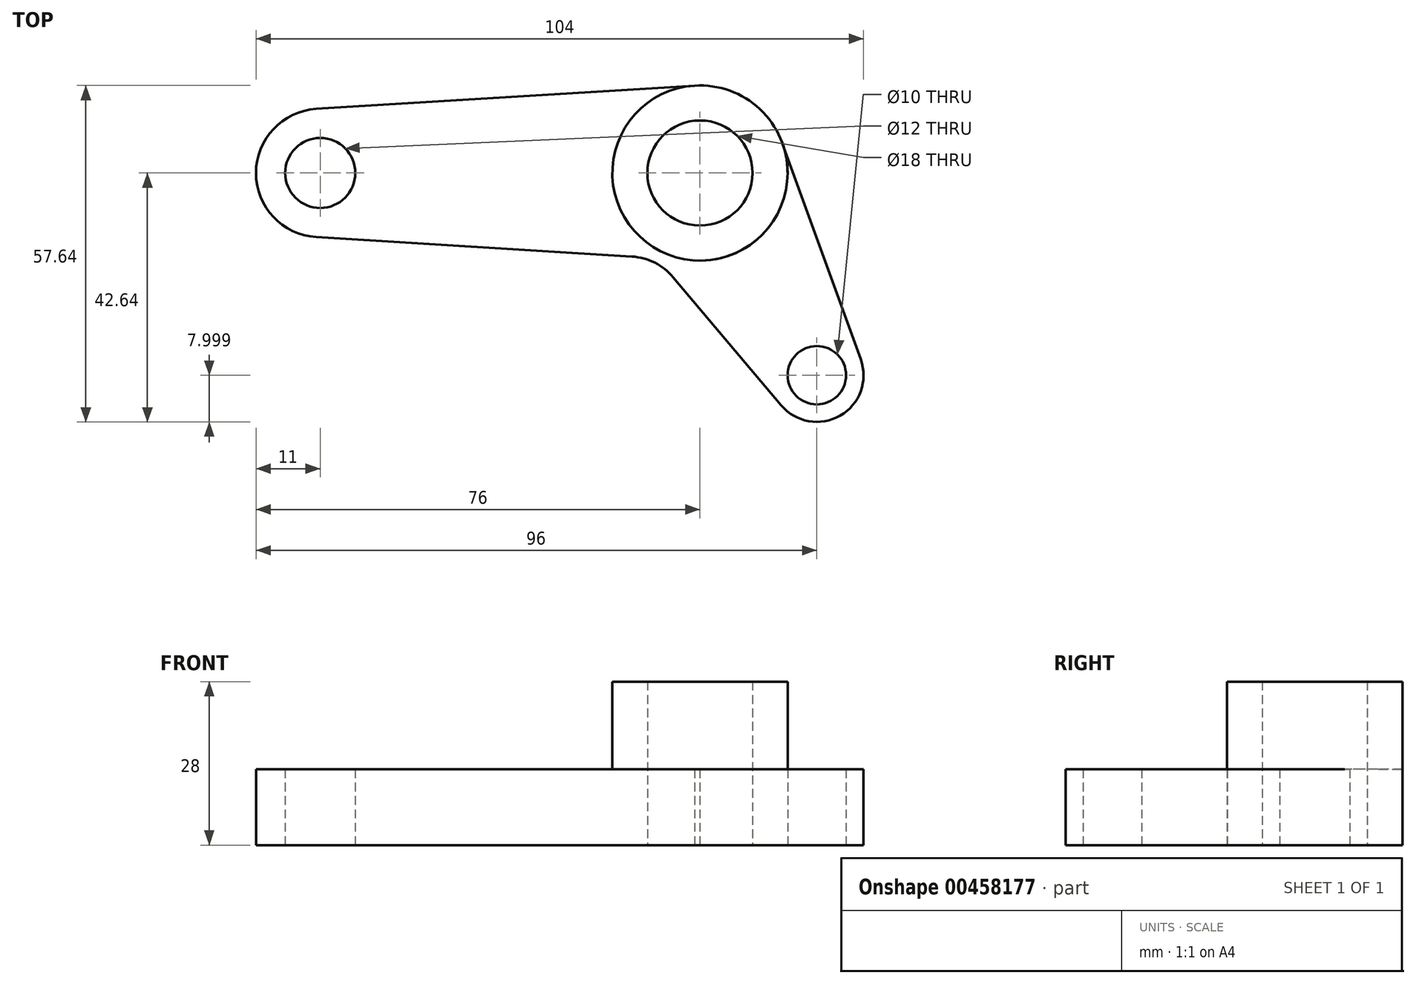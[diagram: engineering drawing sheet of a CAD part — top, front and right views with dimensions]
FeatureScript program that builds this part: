
annotation { "Feature Type Name" : "Feature", "Feature Type Description" : "" }
export const myFeature = defineFeature(function(context is Context, id is Id, definition is map)
    precondition{}
    {
        {
            var Q0;
            Q0=qCreatedBy(makeId("Top.planeOp"),FACE);
            var sketch = newSketch(context, id + "F0", { "sketchPlane" : qUnion([Q0])});
            skCircle(sketch, "E0", {"center": v(0, 0) * mm, "radius": 9 * mm});
            skCircle(sketch, "E1", {"center": v(0, 0) * mm, "radius": 15 * mm});
            skCircle(sketch, "E2", {"center": v(-65, 0) * mm, "radius": 6 * mm});
            skArc(sketch, "E3", {"start": v(-65.68, 10.98) * mm, "mid": v(-76, 0) * mm, "end": v(-65.68, -10.98) * mm});
            skLineSegment(sketch, "E4", {"start": v(-65.68, 10.98) * mm, "end": v(0, 15.03) * mm});
            skLineSegment(sketch, "E5.MirrorCS", {"start": v(-0.92, -14.97) * mm, "end": v(0, -15.03) * mm});
            skCircle(sketch, "E6", {"center": v(20, -34.64) * mm, "radius": 5 * mm});
            skArc(sketch, "E7", {"start": v(13.88, -39.8) * mm, "mid": v(24, -41.57) * mm, "end": v(27.52, -31.92) * mm});
            skLineSegment(sketch, "E8", {"start": v(14.1, 5.11) * mm, "end": v(27.52, -31.92) * mm});
            skLineSegment(sketch, "E9.MirrorCS", {"start": v(-65.68, -10.98) * mm, "end": v(-11.62, -14.31) * mm});
            skLineSegment(sketch, "E10", {"start": v(13.88, -39.8) * mm, "end": v(-4.58, -17.85) * mm});
            skArc(sketch, "E11", {"start": v(-4.58, -17.85) * mm, "mid": v(-7.73, -15.36) * mm, "end": v(-11.62, -14.31) * mm});
            skLineSegment(sketch, "E12.trimOffspring", {"start": v(0, -15) * mm, "end": v(0, -15.03) * mm});
            skSolve(sketch);
        }
        {
            var Q0;
            Q0=makeQuery(id+"F0.imprint","IMPRINT",FACE,{"disambiguationData":[TD([[makeQuery(id+"F0.imprint","IMPRINT",EDGE,{"derivedFrom":sQuery(id+"F0.wireOp",EDGE,"E2")}),-1.0]])]});
            var Q1;
            Q1=makeQuery(id+"F0.imprint","IMPRINT",FACE,{"disambiguationData":[TD([[makeQuery(id+"F0.imprint","IMPRINT",EDGE,{"derivedFrom":sQuery(id+"F0.wireOp",EDGE,"E0")}),-1.0]])]});
            extrude(context, id + "F1", {"entities" : qUnion([Q0, Q1]), "depth" : 28 * mm});
        }
        {
            var Q0;
            Q0=makeQuery(id+"F1.opExtrude","CAP_FACE",FACE,{"disambiguationData":[OSD([sQuery(id+"F0.wireOp",EDGE,"E0"),sQuery(id+"F0.wireOp",EDGE,"E1"),sQuery(id+"F0.wireOp",EDGE,"E2"),sQuery(id+"F0.wireOp",EDGE,"E3"),sQuery(id+"F0.wireOp",EDGE,"E4"),sQuery(id+"F0.wireOp",EDGE,"E6"),sQuery(id+"F0.wireOp",EDGE,"E7"),sQuery(id+"F0.wireOp",EDGE,"E8"),sQuery(id+"F0.wireOp",EDGE,"E9.MirrorCS"),sQuery(id+"F0.wireOp",EDGE,"E10"),sQuery(id+"F0.wireOp",EDGE,"E5.MirrorCS"),sQuery(id+"F0.wireOp",EDGE,"E11"),sQuery(id+"F0.wireOp",EDGE,"E12.trimOffspring")])],"isStart":false});
            var sketch = newSketch(context, id + "F2", { "sketchPlane" : qUnion([Q0])});
            skCircle(sketch, "E13", {"center": v(0, 0) * mm, "radius": 15 * mm});
            skSolve(sketch);
        }
        {
            var Q0;
            Q0=makeQuery(id+"F2.imprint","IMPRINT",FACE,{"disambiguationData":[TD([[makeQuery(id+"F2.imprint","IMPRINT",EDGE,{"derivedFrom":makeQuery(id+"F1.opExtrude","CAP_EDGE",EDGE,{"disambiguationData":[OSD([sQuery(id+"F0.wireOp",EDGE,"E2")])],"isStart":false})}),-1.0]])]});
            extrude(context, id + "F3", {"entities" : qUnion([Q0]), "operationType" : NewBodyOperationType.ADD, "depth" : 10 * mm});
        }
        {
            var Q0;
            Q0=makeQuery(id+"F3.opExtrude","CAP_FACE",FACE,{"disambiguationData":[OSD([sQuery(id+"F0.wireOp",EDGE,"E2"),sQuery(id+"F0.wireOp",EDGE,"E3"),sQuery(id+"F0.wireOp",EDGE,"E4"),sQuery(id+"F0.wireOp",EDGE,"E6"),sQuery(id+"F0.wireOp",EDGE,"E7"),sQuery(id+"F0.wireOp",EDGE,"E8"),sQuery(id+"F0.wireOp",EDGE,"E9.MirrorCS"),sQuery(id+"F0.wireOp",EDGE,"E10"),sQuery(id+"F0.wireOp",EDGE,"E5.MirrorCS"),sQuery(id+"F0.wireOp",EDGE,"E11"),sQuery(id+"F0.wireOp",EDGE,"E12.trimOffspring"),sQuery(id+"F2.wireOp",EDGE,"E13")])],"isStart":false});
            extrude(context, id + "F4", {"entities" : qUnion([Q0]), "operationType" : NewBodyOperationType.REMOVE, "oppositeDirection" : true, "depth" : 25 * mm});
        }
    });
